# Revit family: Trio
name_source: partatom
category: Mechanical Equipment
units: mm (PartAtom-declared; Revit-internal decimal feet)

## family parameters
Always vertical = Yes
Classification = None
Cut with Voids When Loaded = No
Part Type = Normal
Room Calculation Point = No
Round Connector Dimension = Use Diameter
Shared = No
Work Plane-Based = No

## types (2) — shared parameters
00_20_Manufacturer = Blauberg
00_20_Name = Axial fan
Amperage = 0 A
Casing Material = Plastic, opaque, white
Description = For round channels
Frequency = 50 Hz
Load Classification = HVAC
Maintenance zone material = <By Category>
Manufacturer = Blauberg
Number of Fase = 1
URL = https://blaubergventilatoren.de
Voltage = 230 V
e = 23 mm  [stored 0.0754593 ft]
zero-valued in all types: Default Elevation

## per-type parameters (varying)
| type | Apparent Load | Diameter | Dy | H | Height | Length | Maximum Air Flow | Power | Sound pressure level at 3 m distance | Weight | Width | a | c | d |
| Trio 100 | 12 W | 99 mm  [stored 0.324803 ft] | 95 mm | 150 mm | 150 mm | 102 mm | 90.0 m³/h | 8 W | 29 dBA | 0.45 kg | 150 mm | 150 mm | 79 mm | 99 mm  [stored 0.324803 ft] |
| Trio 150 | 48 W | 148 mm  [stored 0.485564 ft] | 144 mm  [stored 0.472441 ft] | 206 mm  [stored 0.675853 ft] | 206 mm  [stored 0.675853 ft] | 123 mm  [stored 0.403543 ft] | 255.0 m³/h | 28 W | 35 dBA | 0.97 kg | 206 mm  [stored 0.675853 ft] | 206 mm  [stored 0.675853 ft] | 100 mm  [stored 0.328084 ft] | 148 mm  [stored 0.485564 ft] |

note: column(s) folded — value = type name in every type: 00_20_Type

note: [stored X ft] marks values corroborated as IEEE doubles in the binary element streams (Revit-internal decimal feet)
